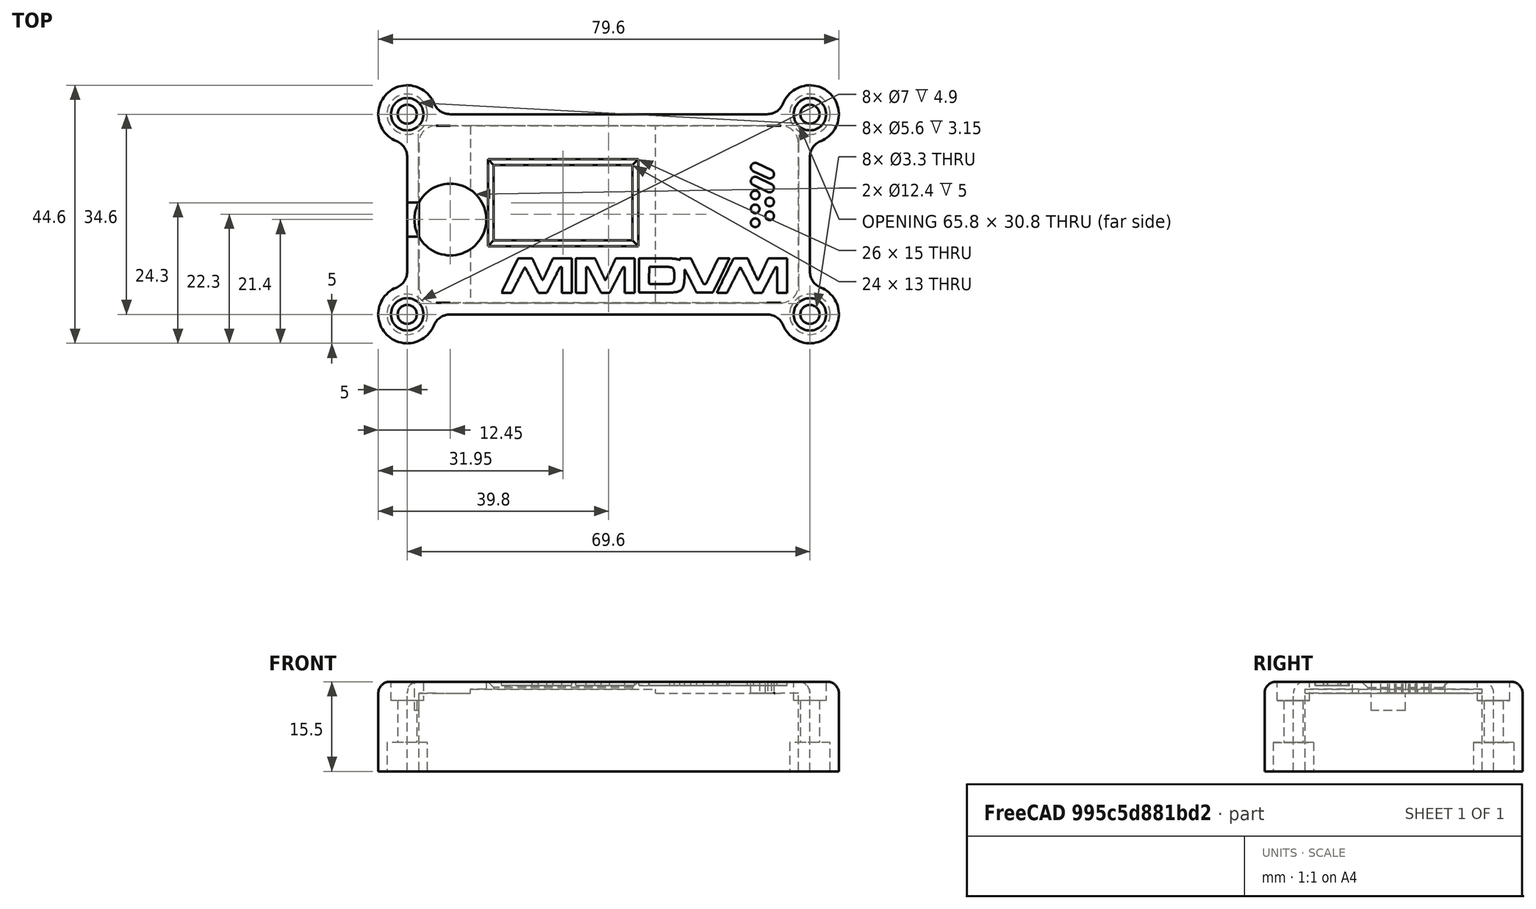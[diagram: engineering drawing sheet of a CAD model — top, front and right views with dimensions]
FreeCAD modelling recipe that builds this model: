
FCSTD DOCUMENT  (FreeCAD 0.18R13830 (Git))
Label: MMDVM_HS_Top-PCB-v1.2-NEW-LEDs
License: CreativeCommons Attribution-NonCommercial-ShareAlike
LicenseURL: http://creativecommons.org/licenses/by-nc-sa/4.0/
objects: Sketcher::SketchObject×11, PartDesign::Pocket×6, Part::Feature×5, PartDesign::Fillet×4, Part::Cut×2, PartDesign::Pad×1, PartDesign::Chamfer×1, PartDesign::Hole×1, Part::MultiFuse×1, Part::FeaturePython×1, Part::Extrusion×1, Mesh::Feature×1, PartDesign::Body×1
note: 43 computed .brp shape members not serialized (recipe doc carries the construction recipe); baked Part::Feature solids carry a one-line shape summary decoded from their .brp

FEATURE [Sketcher::SketchObject] Sketch
  MapMode = 5
  Support = -> [XY_Plane]
  sketch-geometry (24):
    g0: LineSegment [constr] StartX=-32.5 StartY=15 StartZ=0 EndX=32.5 EndY=15 EndZ=0
    g1: LineSegment [constr] StartX=32.5 StartY=15 StartZ=0 EndX=32.5 EndY=-15 EndZ=0
    g2: LineSegment [constr] StartX=32.5 StartY=-15 StartZ=0 EndX=-32.5 EndY=-15 EndZ=0
    g3: LineSegment [constr] StartX=-32.5 StartY=-15 StartZ=0 EndX=-32.5 EndY=15 EndZ=0
    g4: LineSegment [constr] StartX=-29 StartY=11.5 StartZ=0 EndX=29 EndY=11.5 EndZ=0
    g5: LineSegment [constr] StartX=29 StartY=11.5 StartZ=0 EndX=29 EndY=-11.5 EndZ=0
    g6: LineSegment [constr] StartX=29 StartY=-11.5 StartZ=0 EndX=-29 EndY=-11.5 EndZ=0
    g7: LineSegment [constr] StartX=-29 StartY=-11.5 StartZ=0 EndX=-29 EndY=11.5 EndZ=0
    g8: Circle CenterX=-29 CenterY=11.5 CenterZ=0 NormalX=0 NormalY=0 NormalZ=1 AngleXU=0 Radius=1.375
    g9: Circle CenterX=29 CenterY=11.5 CenterZ=0 NormalX=0 NormalY=0 NormalZ=1 AngleXU=0 Radius=1.375
    g10: Circle CenterX=29 CenterY=-11.5 CenterZ=0 NormalX=0 NormalY=0 NormalZ=1 AngleXU=0 Radius=1.375
    g11: Circle CenterX=-29 CenterY=-11.5 CenterZ=0 NormalX=0 NormalY=0 NormalZ=1 AngleXU=0 Radius=1.375
    g12: LineSegment [constr] StartX=-29.5 StartY=12 StartZ=0 EndX=29.5 EndY=12 EndZ=0
    g13: LineSegment [constr] StartX=29.5 StartY=12 StartZ=0 EndX=29.5 EndY=-12 EndZ=0
    g14: LineSegment [constr] StartX=29.5 StartY=-12 StartZ=0 EndX=-29.5 EndY=-12 EndZ=0
    g15: LineSegment [constr] StartX=-29.5 StartY=-12 StartZ=0 EndX=-29.5 EndY=12 EndZ=0
    g16: ArcOfCircle CenterX=-29.5 CenterY=12 CenterZ=0 NormalX=0 NormalY=0 NormalZ=1 AngleXU=0 Radius=3 StartAngle=1.5708 EndAngle=3.1416
    g17: ArcOfCircle CenterX=29.5 CenterY=12 CenterZ=0 NormalX=0 NormalY=0 NormalZ=1 AngleXU=0 Radius=3 StartAngle=1.42077e-07 EndAngle=1.5708
    g18: ArcOfCircle CenterX=29.5 CenterY=-12 CenterZ=0 NormalX=0 NormalY=0 NormalZ=1 AngleXU=0 Radius=3 StartAngle=4.71239 EndAngle=6.28319
    g19: ArcOfCircle CenterX=-29.5 CenterY=-12 CenterZ=0 NormalX=0 NormalY=0 NormalZ=1 AngleXU=0 Radius=3 StartAngle=3.14159 EndAngle=4.71239
    g20: LineSegment StartX=-29.5 StartY=15 StartZ=0 EndX=29.5 EndY=15 EndZ=0
    g21: LineSegment StartX=32.5 StartY=12 StartZ=0 EndX=32.5 EndY=-12 EndZ=0
    g22: LineSegment StartX=29.5 StartY=-15 StartZ=0 EndX=-29.5 EndY=-15 EndZ=0
    g23: LineSegment StartX=-32.5 StartY=-12 StartZ=0 EndX=-32.5 EndY=12 EndZ=0
  constraints (68):
    c: Coincident(g0,g1)
    c: Coincident(g1,g2)
    c: Coincident(g2,g3)
    c: Coincident(g3,g0)
    c: Horizontal(g0)
    c: Horizontal(g2)
    c: Vertical(g1)
    c: Vertical(g3)
    c: DistanceX(g0,g0) = 65
    c: DistanceY(g1,g1) = 30
    c: Symmetric(g0,g0,g-2)
    c: Symmetric(g0,g1,g-1)
    c: Coincident(g4,g5)
    c: Coincident(g5,g6)
    c: Coincident(g6,g7)
    c: Coincident(g7,g4)
    c: Horizontal(g4)
    c: Horizontal(g6)
    c: Vertical(g5)
    c: Vertical(g7)
    c: DistanceX(g4,g4) = 58
    c: DistanceY(g5,g5) = 23
    c: Symmetric(g4,g5,g-1)
    c: Symmetric(g4,g4,g-2)
    c: Coincident(g8,g4)
    c: Coincident(g9,g4)
    c: Coincident(g10,g5)
    c: Coincident(g11,g6)
    c: Radius(g11) = 1.375
    c: Radius(g8) = 1.375
    c: Radius(g9) = 1.375
    c: Radius(g10) = 1.375
    c: Coincident(g12,g13)
    c: Coincident(g13,g14)
    c: Coincident(g14,g15)
    c: Coincident(g15,g12)
    c: Horizontal(g12)
    c: Horizontal(g14)
    c: Vertical(g13)
    c: Vertical(g15)
    c: DistanceX(g4,g12) = 0.5
    c: DistanceY(g4,g12) = 0.5
    c: DistanceY(g13,g5) = 0.5
    c: DistanceX(g14,g6) = 0.5
    c: Coincident(g16,g12)
    c: Radius(g16) = 3
    c: Coincident(g17,g12)
    c: Radius(g17) = 3
    c: Coincident(g18,g13)
    c: Radius(g18) = 3
    c: Coincident(g19,g14)
    c: Radius(g19) = 3
    c: PointOnObject(g16,g0)
    c: PointOnObject(g17,g1)
    c: PointOnObject(g18,g2)
    c: PointOnObject(g19,g3)
    c: Coincident(g20,g16)
    c: Horizontal(g20)
    c: Coincident(g20,g17)
    c: Coincident(g21,g17)
    c: Vertical(g21)
    c: Coincident(g18,g21)
    c: Coincident(g22,g18)
    c: Horizontal(g22)
    c: Coincident(g19,g22)
    c: Coincident(g23,g19)
    c: Vertical(g23)
    c: Coincident(g23,g16)
FEATURE [Sketcher::SketchObject] Sketch001
  MapMode = 5
  Support = -> [XY_Plane]
  expr: Constraints[8] = Sketch.Constraints[8]
  expr: Constraints[41] = Sketch.Constraints[41]
  expr: Constraints[9] = Sketch.Constraints[9]
  expr: Constraints[45] = Sketch.Constraints[45]
  expr: Constraints[43] = Sketch.Constraints[43]
  expr: Constraints[42] = Sketch.Constraints[42]
  expr: Constraints[20] = Sketch.Constraints[20]
  expr: Constraints[21] = Sketch.Constraints[21]
  expr: Constraints[28] = Sketch.Constraints[28]
  expr: Constraints[29] = Sketch.Constraints[29]
  expr: Constraints[30] = Sketch.Constraints[30]
  expr: Constraints[40] = Sketch.Constraints[40]
  expr: Constraints[31] = Sketch.Constraints[31]
  expr: Constraints[47] = Sketch.Constraints[47]
  expr: Constraints[49] = Sketch.Constraints[49]
  expr: Constraints[51] = Sketch.Constraints[51]
  sketch-geometry (64):
    g0: LineSegment [constr] StartX=-32.5 StartY=15 StartZ=0 EndX=32.5 EndY=15 EndZ=0
    g1: LineSegment [constr] StartX=32.5 StartY=15 StartZ=0 EndX=32.5 EndY=-15 EndZ=0
    g2: LineSegment [constr] StartX=32.5 StartY=-15 StartZ=0 EndX=-32.5 EndY=-15 EndZ=0
    g3: LineSegment [constr] StartX=-32.5 StartY=-15 StartZ=0 EndX=-32.5 EndY=15 EndZ=0
    g4: LineSegment [constr] StartX=-29 StartY=11.5 StartZ=0 EndX=29 EndY=11.5 EndZ=0
    g5: LineSegment [constr] StartX=29 StartY=11.5 StartZ=0 EndX=29 EndY=-11.5 EndZ=0
    g6: LineSegment [constr] StartX=29 StartY=-11.5 StartZ=0 EndX=-29 EndY=-11.5 EndZ=0
    g7: LineSegment [constr] StartX=-29 StartY=-11.5 StartZ=0 EndX=-29 EndY=11.5 EndZ=0
    g8: Circle [constr] CenterX=-29 CenterY=11.5 CenterZ=0 NormalX=0 NormalY=0 NormalZ=1 AngleXU=0 Radius=1.375
    g9: Circle [constr] CenterX=29 CenterY=11.5 CenterZ=0 NormalX=0 NormalY=0 NormalZ=1 AngleXU=0 Radius=1.375
    g10: Circle [constr] CenterX=29 CenterY=-11.5 CenterZ=0 NormalX=0 NormalY=0 NormalZ=1 AngleXU=0 Radius=1.375
    g11: Circle [constr] CenterX=-29 CenterY=-11.5 CenterZ=0 NormalX=0 NormalY=0 NormalZ=1 AngleXU=0 Radius=1.375
    g12: LineSegment [constr] StartX=-29.5 StartY=12 StartZ=0 EndX=29.5 EndY=12 EndZ=0
    g13: LineSegment [constr] StartX=29.5 StartY=12 StartZ=0 EndX=29.5 EndY=-12 EndZ=0
    g14: LineSegment [constr] StartX=29.5 StartY=-12 StartZ=0 EndX=-29.5 EndY=-12 EndZ=0
    g15: LineSegment [constr] StartX=-29.5 StartY=-12 StartZ=0 EndX=-29.5 EndY=12 EndZ=0
    g16: ArcOfCircle [constr] CenterX=-29.5 CenterY=12 CenterZ=0 NormalX=0 NormalY=0 NormalZ=1 AngleXU=0 Radius=3 StartAngle=1.5708 EndAngle=3.14159
    g17: ArcOfCircle [constr] CenterX=29.5 CenterY=12 CenterZ=0 NormalX=0 NormalY=0 NormalZ=1 AngleXU=0 Radius=3 StartAngle=2.8425e-08 EndAngle=1.5708
    g18: ArcOfCircle [constr] CenterX=29.5 CenterY=-12 CenterZ=0 NormalX=0 NormalY=0 NormalZ=1 AngleXU=0 Radius=3 StartAngle=4.71239 EndAngle=6.28319
    g19: ArcOfCircle [constr] CenterX=-29.5 CenterY=-12 CenterZ=0 NormalX=0 NormalY=0 NormalZ=1 AngleXU=0 Radius=3 StartAngle=3.14159 EndAngle=4.71239
    g20: LineSegment [constr] StartX=-29.5 StartY=15 StartZ=0 EndX=29.5 EndY=15 EndZ=0
    g21: LineSegment [constr] StartX=32.5 StartY=12 StartZ=0 EndX=32.5 EndY=-12 EndZ=0
    g22: LineSegment [constr] StartX=29.5 StartY=-15 StartZ=0 EndX=-29.5 EndY=-15 EndZ=0
    g23: LineSegment [constr] StartX=-32.5 StartY=-12 StartZ=0 EndX=-32.5 EndY=12 EndZ=0
    g24: ArcOfCircle [constr] CenterX=-29.5 CenterY=12 CenterZ=0 NormalX=0 NormalY=0 NormalZ=1 AngleXU=0 Radius=3.3 StartAngle=1.5708 EndAngle=3.14159
    g25: ArcOfCircle [constr] CenterX=29.5 CenterY=12 CenterZ=0 NormalX=0 NormalY=0 NormalZ=1 AngleXU=0 Radius=3.3 StartAngle=-2.2e-10 EndAngle=1.5708
    g26: ArcOfCircle [constr] CenterX=29.5 CenterY=-12 CenterZ=0 NormalX=0 NormalY=0 NormalZ=1 AngleXU=0 Radius=3.3 StartAngle=4.71239 EndAngle=6.28319
    g27: ArcOfCircle [constr] CenterX=-29.5 CenterY=-12 CenterZ=0 NormalX=0 NormalY=0 NormalZ=1 AngleXU=0 Radius=3.3 StartAngle=3.14159 EndAngle=4.71239
    g28: LineSegment [constr] StartX=-32.8 StartY=12 StartZ=0 EndX=-32.8 EndY=-12 EndZ=0
    g29: LineSegment [constr] StartX=-29.5 StartY=15.3 StartZ=0 EndX=29.5 EndY=15.3 EndZ=0
    g30: LineSegment [constr] StartX=32.8 StartY=12 StartZ=0 EndX=32.8 EndY=-12 EndZ=0
    g31: LineSegment [constr] StartX=29.5 StartY=-15.3 StartZ=0 EndX=-29.5 EndY=-15.3 EndZ=0
    g32: LineSegment [constr] StartX=-34.8 StartY=17.3 StartZ=0 EndX=34.8 EndY=17.3 EndZ=0
    g33: LineSegment [constr] StartX=34.8 StartY=17.3 StartZ=0 EndX=34.8 EndY=-17.3 EndZ=0
    g34: LineSegment [constr] StartX=34.8 StartY=-17.3 StartZ=0 EndX=-34.8 EndY=-17.3 EndZ=0
    g35: LineSegment [constr] StartX=-34.8 StartY=-17.3 StartZ=0 EndX=-34.8 EndY=17.3 EndZ=0
    g36: Circle [constr] CenterX=34.8 CenterY=17.3 CenterZ=0 NormalX=0 NormalY=0 NormalZ=1 AngleXU=0 Radius=5
    g37: Circle [constr] CenterX=34.8 CenterY=-17.3 CenterZ=0 NormalX=0 NormalY=0 NormalZ=1 AngleXU=0 Radius=5
    g38: Circle [constr] CenterX=-34.8 CenterY=-17.3 CenterZ=0 NormalX=0 NormalY=0 NormalZ=1 AngleXU=0 Radius=5
    g39: Circle [constr] CenterX=-34.8 CenterY=17.3 CenterZ=0 NormalX=0 NormalY=0 NormalZ=1 AngleXU=0 Radius=5
    g40: Circle [constr] CenterX=27.3838 CenterY=20.3 CenterZ=0 NormalX=0 NormalY=0 NormalZ=1 AngleXU=0 Radius=3
    g41: Circle [constr] CenterX=-27.3838 CenterY=20.3 CenterZ=0 NormalX=0 NormalY=0 NormalZ=1 AngleXU=0 Radius=3
    g42: Circle [constr] CenterX=-37.8 CenterY=9.8838 CenterZ=0 NormalX=0 NormalY=0 NormalZ=1 AngleXU=0 Radius=3
    g43: Circle [constr] CenterX=-37.8 CenterY=-9.8838 CenterZ=0 NormalX=0 NormalY=0 NormalZ=1 AngleXU=0 Radius=3
    g44: Circle [constr] CenterX=-27.3838 CenterY=-20.3 CenterZ=0 NormalX=0 NormalY=0 NormalZ=1 AngleXU=0 Radius=3
    g45: Circle [constr] CenterX=27.3838 CenterY=-20.3 CenterZ=0 NormalX=0 NormalY=0 NormalZ=1 AngleXU=0 Radius=3
    g46: Circle [constr] CenterX=37.8 CenterY=-9.8838 CenterZ=0 NormalX=0 NormalY=0 NormalZ=1 AngleXU=0 Radius=3
    g47: Circle [constr] CenterX=37.8 CenterY=9.8838 CenterZ=0 NormalX=0 NormalY=0 NormalZ=1 AngleXU=0 Radius=3
    g48: ArcOfCircle CenterX=34.8 CenterY=17.3 CenterZ=0 NormalX=0 NormalY=0 NormalZ=1 AngleXU=0 Radius=5 StartAngle=5.09679 EndAngle=9.04038
    g49: ArcOfCircle CenterX=27.3838 CenterY=20.3 CenterZ=0 NormalX=0 NormalY=0 NormalZ=1 AngleXU=0 Radius=3 StartAngle=4.71239 EndAngle=5.89879
    g50: ArcOfCircle CenterX=37.8 CenterY=9.8838 CenterZ=0 NormalX=0 NormalY=0 NormalZ=1 AngleXU=0 Radius=3 StartAngle=1.95519 EndAngle=3.14159
    g51: ArcOfCircle CenterX=37.8 CenterY=-9.8838 CenterZ=0 NormalX=0 NormalY=0 NormalZ=1 AngleXU=0 Radius=3 StartAngle=3.14159 EndAngle=4.32799
    g52: ArcOfCircle CenterX=34.8 CenterY=-17.3 CenterZ=0 NormalX=0 NormalY=0 NormalZ=1 AngleXU=0 Radius=5 StartAngle=3.52599 EndAngle=7.46958
    g53: ArcOfCircle CenterX=27.3838 CenterY=-20.3 CenterZ=0 NormalX=0 NormalY=0 NormalZ=1 AngleXU=0 Radius=3 StartAngle=0.384397 EndAngle=1.5708
    g54: ArcOfCircle CenterX=-27.3838 CenterY=-20.3 CenterZ=0 NormalX=0 NormalY=0 NormalZ=1 AngleXU=0 Radius=3 StartAngle=1.5708 EndAngle=2.7572
    g55: ArcOfCircle CenterX=-34.8 CenterY=-17.3 CenterZ=0 NormalX=0 NormalY=0 NormalZ=1 AngleXU=0 Radius=5 StartAngle=1.95519 EndAngle=5.89879
    g56: ArcOfCircle CenterX=-37.8 CenterY=-9.8838 CenterZ=0 NormalX=0 NormalY=0 NormalZ=1 AngleXU=0 Radius=3 StartAngle=5.09679 EndAngle=6.28319
    g57: ArcOfCircle CenterX=-37.8 CenterY=9.8838 CenterZ=0 NormalX=0 NormalY=0 NormalZ=1 AngleXU=0 Radius=3 StartAngle=6.28319 EndAngle=7.46958
    g58: ArcOfCircle CenterX=-34.8 CenterY=17.3 CenterZ=0 NormalX=0 NormalY=0 NormalZ=1 AngleXU=0 Radius=5 StartAngle=0.384397 EndAngle=4.32799
    g59: ArcOfCircle CenterX=-27.3838 CenterY=20.3 CenterZ=0 NormalX=0 NormalY=0 NormalZ=1 AngleXU=0 Radius=3 StartAngle=3.52599 EndAngle=4.71239
    g60: LineSegment StartX=-27.3838 StartY=17.3 StartZ=0 EndX=27.3838 EndY=17.3 EndZ=0
    g61: LineSegment StartX=34.8 StartY=9.8838 StartZ=0 EndX=34.8 EndY=-9.8838 EndZ=0
    g62: LineSegment StartX=27.3838 StartY=-17.3 StartZ=0 EndX=-27.3838 EndY=-17.3 EndZ=0
    g63: LineSegment StartX=-34.8 StartY=-9.8838 StartZ=0 EndX=-34.8 EndY=9.8838 EndZ=0
  constraints (184):
    c: Coincident(g0,g1)
    c: Coincident(g1,g2)
    c: Coincident(g2,g3)
    c: Coincident(g3,g0)
    c: Horizontal(g0)
    c: Horizontal(g2)
    c: Vertical(g1)
    c: Vertical(g3)
    c: DistanceX(g0,g0) = 65
    c: DistanceY(g1,g1) = 30
    c: Symmetric(g0,g0,g-2)
    c: Symmetric(g0,g1,g-1)
    c: Coincident(g4,g5)
    c: Coincident(g5,g6)
    c: Coincident(g6,g7)
    c: Coincident(g7,g4)
    c: Horizontal(g4)
    c: Horizontal(g6)
    c: Vertical(g5)
    c: Vertical(g7)
    c: DistanceX(g4,g4) = 58
    c: DistanceY(g5,g5) = 23
    c: Symmetric(g4,g5,g-1)
    c: Symmetric(g4,g4,g-2)
    c: Coincident(g8,g4)
    c: Coincident(g9,g4)
    c: Coincident(g10,g5)
    c: Coincident(g11,g6)
    c: Radius(g11) = 1.375
    c: Radius(g8) = 1.375
    c: Radius(g9) = 1.375
    c: Radius(g10) = 1.375
    c: Coincident(g12,g13)
    c: Coincident(g13,g14)
    c: Coincident(g14,g15)
    c: Coincident(g15,g12)
    c: Horizontal(g12)
    c: Horizontal(g14)
    c: Vertical(g13)
    c: Vertical(g15)
    c: DistanceX(g4,g12) = 0.5
    c: DistanceY(g4,g12) = 0.5
    c: DistanceY(g13,g5) = 0.5
    c: DistanceX(g14,g6) = 0.5
    c: Coincident(g16,g12)
    c: Radius(g16) = 3
    c: Coincident(g17,g12)
    c: Radius(g17) = 3
    c: Coincident(g18,g13)
    c: Radius(g18) = 3
    c: Coincident(g19,g14)
    c: Radius(g19) = 3
    c: PointOnObject(g16,g0)
    c: PointOnObject(g17,g1)
    c: PointOnObject(g18,g2)
    c: PointOnObject(g19,g3)
    c: Coincident(g20,g16)
    c: Horizontal(g20)
    c: Coincident(g20,g17)
    c: Coincident(g21,g17)
    c: Vertical(g21)
    c: Coincident(g18,g21)
    c: Coincident(g22,g18)
    c: Horizontal(g22)
    c: Coincident(g19,g22)
    c: Coincident(g23,g19)
    c: Vertical(g23)
    c: Coincident(g23,g16)
    c: Coincident(g24,g12)
    c: Radius(g24) = 3.3
    c: Coincident(g25,g12)
    c: Radius(g25) = 3.3
    c: Coincident(g26,g13)
    c: Radius(g26) = 3.3
    c: Coincident(g27,g14)
    c: Radius(g27) = 3.3
    c: Vertical(g28)
    c: DistanceX(g28,g2) = 0.3
    c: Coincident(g27,g28)
    c: Coincident(g28,g24)
    c: Horizontal(g29)
    c: DistanceY(g0,g29) = 0.3
    c: Coincident(g24,g29)
    c: Coincident(g25,g29)
    c: Vertical(g30)
    c: DistanceX(g0,g30) = 0.3
    c: Coincident(g25,g30)
    c: Coincident(g30,g26)
    c: Horizontal(g31)
    c: DistanceY(g31,g1) = 0.3
    c: Coincident(g31,g26)
    c: Coincident(g31,g27)
    c: Coincident(g32,g33)
    c: Coincident(g33,g34)
    c: Coincident(g34,g35)
    c: Coincident(g35,g32)
    c: Horizontal(g32)
    c: Horizontal(g34)
    c: Vertical(g33)
    c: Vertical(g35)
    c: DistanceY(g25,g32) = 2
    c: DistanceX(g25,g32) = 2
    c: DistanceY(g33,g26) = 2
    c: DistanceX(g34,g27) = 2
    c: Coincident(g36,g32)
    c: Coincident(g37,g33)
    c: Coincident(g38,g34)
    c: Coincident(g39,g32)
    c: Radius(g39) = 5
    c: Radius(g38) = 5
    c: Radius(g37) = 5
    c: Radius(g36) = 5
    c: Radius(g40) = 3
    c: Tangent(g40,g36)
    c: Tangent(g40,g32)
    c: Tangent(g47,g36)
    c: Radius(g47) = 3
    c: Tangent(g47,g33)
    c: Radius(g46) = 3
    c: Tangent(g46,g37)
    c: Tangent(g46,g33)
    c: Radius(g45) = 3
    c: Tangent(g45,g37)
    c: Tangent(g45,g34)
    c: Radius(g44) = 3
    c: Tangent(g44,g34)
    c: Tangent(g44,g38)
    c: Radius(g43) = 3
    c: Tangent(g43,g38)
    c: Tangent(g43,g35)
    c: Radius(g42) = 3
    c: Tangent(g42,g35)
    c: Tangent(g42,g39)
    c: Radius(g41) = 3
    c: Tangent(g41,g32)
    c: Tangent(g41,g39)
    c: Coincident(g48,g32)
    c: PointOnObject(g48,g36)
    c: Coincident(g49,g40)
    c: PointOnObject(g49,g40)
    c: Coincident(g50,g47)
    c: PointOnObject(g50,g47)
    c: Coincident(g51,g46)
    c: PointOnObject(g51,g46)
    c: Coincident(g52,g33)
    c: PointOnObject(g52,g37)
    c: Coincident(g53,g45)
    c: PointOnObject(g53,g45)
    c: Coincident(g54,g44)
    c: PointOnObject(g54,g44)
    c: Coincident(g55,g34)
    c: PointOnObject(g55,g38)
    c: Coincident(g56,g43)
    c: PointOnObject(g56,g43)
    c: Coincident(g57,g42)
    c: PointOnObject(g57,g42)
    c: Coincident(g58,g32)
    c: PointOnObject(g58,g39)
    c: Coincident(g59,g41)
    c: PointOnObject(g59,g41)
    c: Coincident(g49,g48)
    c: Coincident(g48,g50)
    c: Coincident(g51,g52)
    c: Coincident(g52,g53)
    c: Coincident(g54,g55)
    c: Coincident(g55,g56)
    c: Coincident(g57,g58)
    c: Coincident(g58,g59)
    c: PointOnObject(g60,g32)
    c: Horizontal(g60)
    c: PointOnObject(g61,g33)
    c: Vertical(g61)
    c: PointOnObject(g62,g34)
    c: Horizontal(g62)
    c: PointOnObject(g63,g35)
    c: Vertical(g63)
    c: Coincident(g59,g60)
    c: Coincident(g60,g49)
    c: Coincident(g50,g61)
    c: Coincident(g61,g51)
    c: Coincident(g53,g62)
    c: Coincident(g54,g62)
    c: Coincident(g56,g63)
    c: Coincident(g57,g63)
FEATURE [PartDesign::Pad] Pad
  Length = 15.5
  Length2 = 100
  Profile = -> Sketch001
  Type = 0
FEATURE [Sketcher::SketchObject] Sketch002
  ExternalGeometry = -> [Pad]
  MapMode = 5
  Placement = pos=(0,0,0) rot=(1,0,0;3.14159rad)
  Support = -> [Pad]
  sketch-geometry (4):
    g0: Circle CenterX=34.8 CenterY=17.3 CenterZ=0 NormalX=0 NormalY=0 NormalZ=1 AngleXU=0 Radius=3.5
    g1: Circle CenterX=34.8 CenterY=-17.3 CenterZ=0 NormalX=0 NormalY=0 NormalZ=1 AngleXU=0 Radius=3.5
    g2: Circle CenterX=-34.8 CenterY=-17.3 CenterZ=0 NormalX=0 NormalY=0 NormalZ=1 AngleXU=0 Radius=3.5
    g3: Circle CenterX=-34.8 CenterY=17.3 CenterZ=0 NormalX=0 NormalY=0 NormalZ=1 AngleXU=0 Radius=3.5
  constraints (8):
    c: Coincident(g0,g-3)
    c: Radius(g0) = 3.5
    c: Coincident(g1,g-6)
    c: Radius(g1) = 3.5
    c: Coincident(g2,g-5)
    c: Radius(g2) = 3.5
    c: Coincident(g3,g-4)
    c: Radius(g3) = 3.5
FEATURE [PartDesign::Pocket] Pocket
  BaseFeature = -> Pad
  Length = 5
  Length2 = 100
  Profile = -> Sketch002
  Type = 0
FEATURE [Sketcher::SketchObject] Sketch003
  MapMode = 5
  Placement = pos=(0,0,0) rot=(1,0,0;3.14159rad)
  Support = -> [Pocket]
  expr: Constraints[8] = Sketch.Constraints[8]
  expr: Constraints[39] = Sketch.Constraints[40]
  expr: Constraints[30] = Sketch.Constraints[31]
  expr: Constraints[27] = Sketch.Constraints[28]
  expr: Constraints[29] = Sketch.Constraints[30]
  expr: Constraints[28] = Sketch.Constraints[29]
  expr: Constraints[20] = -Sketch.Constraints[21]
  expr: Constraints[19] = Sketch.Constraints[20]
  expr: Constraints[42] = Sketch.Constraints[43]
  expr: Constraints[41] = -Sketch.Constraints[42]
  expr: Constraints[9] = -Sketch.Constraints[9]
  expr: Constraints[40] = -Sketch.Constraints[41]
  sketch-geometry (32):
    g0: LineSegment [constr] StartX=-32.5 StartY=-15 StartZ=0 EndX=32.5 EndY=-15 EndZ=0
    g1: LineSegment [constr] StartX=32.5 StartY=-15 StartZ=0 EndX=32.5 EndY=15 EndZ=0
    g2: LineSegment [constr] StartX=32.5 StartY=15 StartZ=0 EndX=-32.5 EndY=15 EndZ=0
    g3: LineSegment [constr] StartX=-32.5 StartY=15 StartZ=0 EndX=-32.5 EndY=-15 EndZ=0
    g4: LineSegment [constr] StartX=-29 StartY=-11.5 StartZ=0 EndX=29 EndY=-11.5 EndZ=0
    g5: LineSegment [constr] StartX=29 StartY=-11.5 StartZ=0 EndX=29 EndY=11.5 EndZ=0
    g6: LineSegment [constr] StartX=29 StartY=11.5 StartZ=0 EndX=-29 EndY=11.5 EndZ=0
    g7: LineSegment [constr] StartX=-29 StartY=11.5 StartZ=0 EndX=-29 EndY=-11.5 EndZ=0
    g8: Circle [constr] CenterX=-29 CenterY=-11.5 CenterZ=0 NormalX=0 NormalY=0 NormalZ=1 AngleXU=0 Radius=1.375
    g9: Circle [constr] CenterX=29 CenterY=-11.5 CenterZ=0 NormalX=0 NormalY=0 NormalZ=1 AngleXU=0 Radius=1.375
    g10: Circle [constr] CenterX=29 CenterY=11.5 CenterZ=0 NormalX=0 NormalY=0 NormalZ=1 AngleXU=0 Radius=1.375
    g11: Circle [constr] CenterX=-29 CenterY=11.5 CenterZ=0 NormalX=0 NormalY=0 NormalZ=1 AngleXU=0 Radius=1.375
    g12: LineSegment [constr] StartX=-29.5 StartY=-12 StartZ=0 EndX=29.5 EndY=-12 EndZ=0
    g13: LineSegment [constr] StartX=29.5 StartY=-12 StartZ=0 EndX=29.5 EndY=12 EndZ=0
    g14: LineSegment [constr] StartX=29.5 StartY=12 StartZ=0 EndX=-29.5 EndY=12 EndZ=0
    g15: LineSegment [constr] StartX=-29.5 StartY=12 StartZ=0 EndX=-29.5 EndY=-12 EndZ=0
    g16: LineSegment [constr] StartX=-29.5121 StartY=-15 StartZ=0 EndX=29.5 EndY=-15 EndZ=0
    g17: LineSegment [constr] StartX=32.5 StartY=-12 StartZ=0 EndX=32.5 EndY=12 EndZ=0
    g18: LineSegment [constr] StartX=29.5 StartY=15 StartZ=0 EndX=-29.5121 EndY=15 EndZ=0
    g19: LineSegment [constr] StartX=-32.5 StartY=12 StartZ=0 EndX=-32.5 EndY=-12 EndZ=0
    g20: ArcOfCircle [constr] CenterX=-29.5 CenterY=12 CenterZ=0 NormalX=0 NormalY=0 NormalZ=1 AngleXU=0 Radius=3.00002 StartAngle=1.57483 EndAngle=3.1416
    g21: ArcOfCircle [constr] CenterX=29.5 CenterY=12 CenterZ=0 NormalX=0 NormalY=0 NormalZ=1 AngleXU=0 Radius=3 StartAngle=6.28318 EndAngle=7.85399
    g22: ArcOfCircle [constr] CenterX=29.5 CenterY=-12 CenterZ=0 NormalX=0 NormalY=0 NormalZ=1 AngleXU=0 Radius=3 StartAngle=4.71238 EndAngle=6.28319
    g23: ArcOfCircle [constr] CenterX=-29.5 CenterY=-12 CenterZ=0 NormalX=0 NormalY=0 NormalZ=1 AngleXU=0 Radius=3.00002 StartAngle=3.14159 EndAngle=4.70836
    g24: LineSegment StartX=-29.8 StartY=15.3 StartZ=0 EndX=29.8 EndY=15.3 EndZ=0
    g25: LineSegment StartX=32.8 StartY=12.3 StartZ=0 EndX=32.8 EndY=-12.3 EndZ=0
    g26: LineSegment StartX=29.8 StartY=-15.3 StartZ=0 EndX=-29.8 EndY=-15.3 EndZ=0
    g27: LineSegment StartX=-32.8 StartY=-12.3 StartZ=0 EndX=-32.8 EndY=12.3 EndZ=0
    g28: ArcOfCircle CenterX=29.8 CenterY=12.3 CenterZ=0 NormalX=0 NormalY=0 NormalZ=1 AngleXU=0 Radius=3 StartAngle=0 EndAngle=1.5708
    g29: ArcOfCircle CenterX=29.8 CenterY=-12.3 CenterZ=0 NormalX=0 NormalY=0 NormalZ=1 AngleXU=0 Radius=3 StartAngle=4.71239 EndAngle=6.28319
    g30: ArcOfCircle CenterX=-29.8 CenterY=-12.3 CenterZ=0 NormalX=0 NormalY=0 NormalZ=1 AngleXU=0 Radius=3 StartAngle=3.14159 EndAngle=4.71239
    g31: ArcOfCircle CenterX=-29.8 CenterY=12.3 CenterZ=0 NormalX=0 NormalY=0 NormalZ=1 AngleXU=0 Radius=3 StartAngle=1.5708 EndAngle=3.14159
  constraints (83):
    c: Coincident(g0,g1)
    c: Coincident(g1,g2)
    c: Coincident(g2,g3)
    c: Coincident(g3,g0)
    c: Horizontal(g0)
    c: Horizontal(g2)
    c: Vertical(g1)
    c: Vertical(g3)
    c: DistanceX(g0,g0) = 65
    c: DistanceY(g1,g1) = -30
    c: Symmetric(g0,g0,g-2)
    c: Symmetric(g0,g1,g-1)
    c: Coincident(g4,g5)
    c: Coincident(g5,g6)
    c: Coincident(g6,g7)
    c: Horizontal(g4)
    c: Horizontal(g6)
    c: Vertical(g5)
    c: Vertical(g7)
    c: DistanceX(g4,g4) = 58
    c: DistanceY(g5,g5) = -23
    c: Symmetric(g4,g5,g-1)
    c: Symmetric(g4,g4,g-2)
    c: Coincident(g8,g4)
    c: Coincident(g9,g4)
    c: Coincident(g10,g5)
    c: Coincident(g11,g6)
    c: Radius(g11) = 1.375
    c: Radius(g8) = 1.375
    c: Radius(g9) = 1.375
    c: Radius(g10) = 1.375
    c: Coincident(g12,g13)
    c: Coincident(g13,g14)
    c: Coincident(g14,g15)
    c: Coincident(g15,g12)
    c: Horizontal(g12)
    c: Horizontal(g14)
    c: Vertical(g13)
    c: Vertical(g15)
    c: DistanceX(g4,g12) = 0.5
    c: DistanceY(g4,g12) = -0.5
    c: DistanceY(g13,g5) = -0.5
    c: DistanceX(g14,g6) = 0.5
    c: PointOnObject(g16,g0)
    c: PointOnObject(g17,g1)
    c: PointOnObject(g18,g2)
    c: PointOnObject(g19,g3)
    c: Horizontal(g16)
    c: Vertical(g17)
    c: Horizontal(g18)
    c: Vertical(g19)
    c: Coincident(g20,g14)
    c: Coincident(g20,g18)
    c: Coincident(g20,g19)
    c: Coincident(g21,g13)
    c: Coincident(g21,g17)
    c: Coincident(g21,g18)
    c: Coincident(g22,g12)
    c: Coincident(g22,g16)
    c: Coincident(g22,g17)
    c: Coincident(g23,g12)
    c: Coincident(g23,g19)
    c: Coincident(g23,g16)
    c: Horizontal(g24)
    c: Horizontal(g26)
    c: Vertical(g25)
    c: Vertical(g27)
    c: Tangent(g24,g28) = 1.5708
    c: Tangent(g25,g28) = 1.5708
    c: Tangent(g25,g29) = 1.5708
    c: Tangent(g26,g29) = 1.5708
    c: Tangent(g26,g30) = 1.5708
    c: Tangent(g27,g30) = 1.5708
    c: Tangent(g27,g31) = 1.5708
    c: Tangent(g24,g31) = 1.5708
    c: Radius(g31) = 3
    c: Radius(g28) = 3
    c: Radius(g29) = 3
    c: Radius(g30) = 3
    c: DistanceY(g1,g24) = 0.3
    c: DistanceX(g17,g25) = 0.3
    c: DistanceY(g26,g16) = 0.3
    c: DistanceX(g27,g19) = 0.3
FEATURE [PartDesign::Pocket] Pocket001
  BaseFeature = -> Pocket
  Length = 13.5
  Length2 = 100
  Profile = -> Sketch003
  Type = 0
FEATURE [Sketcher::SketchObject] Sketch004
  ExternalGeometry = -> [Pocket001]
  MapMode = 5
  Placement = pos=(0,0,15.5) rot=(0,0,1;0rad)
  Support = -> [Pocket001]
  sketch-geometry (32):
    g0: LineSegment StartX=-27.3838 StartY=17.3 StartZ=0 EndX=-31.8 EndY=17.3 EndZ=0
    g1: LineSegment StartX=-34.8 StartY=9.8838 StartZ=0 EndX=-34.8 EndY=14.3 EndZ=0
    g2: Circle [constr] CenterX=-31.8 CenterY=14.3 CenterZ=0 NormalX=0 NormalY=0 NormalZ=1 AngleXU=0 Radius=3
    g3: ArcOfCircle CenterX=-31.8 CenterY=14.3 CenterZ=0 NormalX=0 NormalY=0 NormalZ=1 AngleXU=0 Radius=3 StartAngle=1.5708 EndAngle=3.14159
    g4: LineSegment StartX=-41.7809 StartY=24.2149 StartZ=0 EndX=-27.3838 EndY=24.2149 EndZ=0
    g5: LineSegment StartX=-41.7809 StartY=9.8838 StartZ=0 EndX=-41.7809 EndY=24.2149 EndZ=0
    g6: LineSegment StartX=-27.3838 StartY=24.2149 StartZ=0 EndX=-27.3838 EndY=17.3 EndZ=0
    g7: LineSegment StartX=-41.7809 StartY=9.8838 StartZ=0 EndX=-34.8 EndY=9.8838 EndZ=0
    g8: LineSegment StartX=27.3838 StartY=17.3 StartZ=0 EndX=31.8 EndY=17.3 EndZ=0
    g9: LineSegment StartX=34.8 StartY=9.8838 StartZ=0 EndX=34.8 EndY=14.3 EndZ=0
    g10: Circle [constr] CenterX=31.8 CenterY=14.3 CenterZ=0 NormalX=0 NormalY=0 NormalZ=1 AngleXU=0 Radius=3
    g11: ArcOfCircle CenterX=31.8 CenterY=14.3 CenterZ=0 NormalX=0 NormalY=0 NormalZ=1 AngleXU=0 Radius=3 StartAngle=4.4834e-08 EndAngle=1.5708
    g12: LineSegment StartX=41.7622 StartY=24.6512 StartZ=0 EndX=27.3838 EndY=24.6512 EndZ=0
    g13: LineSegment StartX=41.7622 StartY=9.8838 StartZ=0 EndX=41.7622 EndY=24.6512 EndZ=0
    g14: LineSegment StartX=27.3838 StartY=24.6512 StartZ=0 EndX=27.3838 EndY=17.3 EndZ=0
    g15: LineSegment StartX=41.7622 StartY=9.8838 StartZ=0 EndX=34.8 EndY=9.8838 EndZ=0
    g16: LineSegment StartX=-34.8 StartY=-9.8838 StartZ=0 EndX=-34.8 EndY=-14.3 EndZ=0
    g17: LineSegment StartX=-27.3838 StartY=-17.3 StartZ=0 EndX=-31.8 EndY=-17.3 EndZ=0
    g18: Circle [constr] CenterX=-31.8 CenterY=-14.3 CenterZ=0 NormalX=0 NormalY=0 NormalZ=1 AngleXU=0 Radius=3
    g19: ArcOfCircle CenterX=-31.8 CenterY=-14.3 CenterZ=0 NormalX=0 NormalY=0 NormalZ=1 AngleXU=0 Radius=3 StartAngle=3.14159 EndAngle=4.71239
    g20: LineSegment StartX=-27.3838 StartY=-24.2044 StartZ=0 EndX=-41.4724 EndY=-24.2044 EndZ=0
    g21: LineSegment StartX=-41.4724 StartY=-24.2044 StartZ=0 EndX=-41.4724 EndY=-9.8838 EndZ=0
    g22: LineSegment StartX=-41.4724 StartY=-9.8838 StartZ=0 EndX=-34.8 EndY=-9.8838 EndZ=0
    g23: LineSegment StartX=-27.3838 StartY=-24.2044 StartZ=0 EndX=-27.3838 EndY=-17.3 EndZ=0
    g24: LineSegment StartX=34.8 StartY=-9.8838 StartZ=0 EndX=34.8 EndY=-14.3 EndZ=0
    g25: LineSegment StartX=27.3838 StartY=-17.3 StartZ=0 EndX=31.8 EndY=-17.3 EndZ=0
    g26: Circle [constr] CenterX=31.8 CenterY=-14.3 CenterZ=0 NormalX=0 NormalY=0 NormalZ=1 AngleXU=0 Radius=3
    g27: ArcOfCircle CenterX=31.8 CenterY=-14.3 CenterZ=0 NormalX=0 NormalY=0 NormalZ=1 AngleXU=0 Radius=3 StartAngle=4.71239 EndAngle=6.28319
    g28: LineSegment StartX=41.5436 StartY=-23.6904 StartZ=0 EndX=27.3838 EndY=-23.6904 EndZ=0
    g29: LineSegment StartX=41.5436 StartY=-9.8838 StartZ=0 EndX=41.5436 EndY=-23.6904 EndZ=0
    g30: LineSegment StartX=41.5436 StartY=-9.8838 StartZ=0 EndX=34.8 EndY=-9.8838 EndZ=0
    g31: LineSegment StartX=27.3838 StartY=-23.6904 StartZ=0 EndX=27.3838 EndY=-17.3 EndZ=0
  constraints (88):
    c: PointOnObject(g0,g-3)
    c: Horizontal(g0)
    c: PointOnObject(g1,g-6)
    c: Vertical(g1)
    c: Radius(g2) = 3
    c: Tangent(g2,g0)
    c: Tangent(g2,g1)
    c: Coincident(g3,g2)
    c: PointOnObject(g3,g2)
    c: Coincident(g3,g1)
    c: Coincident(g3,g0)
    c: Coincident(g5,g4)
    c: Horizontal(g4)
    c: Vertical(g5)
    c: Coincident(g6,g4)
    c: Vertical(g6)
    c: Coincident(g7,g5)
    c: Horizontal(g7)
    c: Coincident(g7,g1)
    c: Coincident(g6,g0)
    c: PointOnObject(g8,g-3)
    c: Horizontal(g8)
    c: PointOnObject(g9,g-4)
    c: Vertical(g9)
    c: Radius(g10) = 3
    c: Tangent(g10,g8)
    c: Tangent(g10,g9)
    c: Coincident(g11,g10)
    c: PointOnObject(g11,g10)
    c: Coincident(g11,g8)
    c: Coincident(g11,g9)
    c: Coincident(g13,g12)
    c: Horizontal(g12)
    c: Vertical(g13)
    c: Coincident(g14,g12)
    c: Vertical(g14)
    c: Coincident(g15,g13)
    c: Horizontal(g15)
    c: Coincident(g15,g9)
    c: Coincident(g14,g8)
    c: PointOnObject(g16,g-6)
    c: Vertical(g16)
    c: PointOnObject(g17,g-5)
    c: Horizontal(g17)
    c: Radius(g18) = 3
    c: Tangent(g18,g16)
    c: Tangent(g18,g17)
    c: Coincident(g19,g18)
    c: PointOnObject(g19,g18)
    c: Coincident(g19,g17)
    c: Coincident(g19,g16)
    c: Coincident(g20,g21)
    c: Horizontal(g20)
    c: Vertical(g21)
    c: Coincident(g22,g21)
    c: Horizontal(g22)
    c: Coincident(g23,g20)
    c: Vertical(g23)
    c: Coincident(g23,g17)
    c: Coincident(g22,g16)
    c: PointOnObject(g24,g-4)
    c: Vertical(g24)
    c: PointOnObject(g25,g-5)
    c: Horizontal(g25)
    c: Radius(g26) = 3
    c: Tangent(g26,g24)
    c: Tangent(g26,g25)
    c: Coincident(g27,g26)
    c: PointOnObject(g27,g26)
    c: Coincident(g27,g24)
    c: Coincident(g27,g25)
    c: Coincident(g29,g28)
    c: Horizontal(g28)
    c: Vertical(g29)
    c: Coincident(g30,g29)
    c: Horizontal(g30)
    c: Coincident(g31,g28)
    c: Vertical(g31)
    c: Coincident(g31,g25)
    c: Coincident(g30,g24)
    c: Coincident(g0,g-3)
    c: Coincident(g1,g-6)
    c: Coincident(g-6,g16)
    c: Coincident(g17,g-5)
    c: Coincident(g-5,g25)
    c: Coincident(g-4,g24)
    c: Coincident(g9,g-4)
    c: Coincident(g8,g-3)
FEATURE [Sketcher::SketchObject] Sketch005
  ExternalGeometry = -> [Pocket001,Sketch]
  MapMode = 5
  Placement = pos=(0,0,15.5) rot=(0,0,1;0rad)
  Support = -> [Pocket001]
  sketch-geometry (10):
    g0: LineSegment [constr] StartX=-27.35 StartY=31.2328 StartZ=0 EndX=-27.35 EndY=-27.0552 EndZ=0
    g1: LineSegment [constr] StartX=-45.4064 StartY=-0.9 StartZ=0 EndX=40.4454 EndY=-0.9 EndZ=0
    g2: Circle [constr] CenterX=-27.35 CenterY=-0.9 CenterZ=0 NormalX=0 NormalY=0 NormalZ=1 AngleXU=0 Radius=6.2
    g3: LineSegment StartX=-19.85 StartY=8.5 StartZ=0 EndX=4.15 EndY=8.5 EndZ=0
    g4: LineSegment StartX=4.15 StartY=8.5 StartZ=0 EndX=4.15 EndY=-4.5 EndZ=0
    g5: LineSegment StartX=4.15 StartY=-4.5 StartZ=0 EndX=-19.85 EndY=-4.5 EndZ=0
    g6: LineSegment StartX=-19.85 StartY=-4.5 StartZ=0 EndX=-19.85 EndY=8.5 EndZ=0
    g7: LineSegment [constr] StartX=-29 StartY=24.9491 StartZ=0 EndX=-29 EndY=-20.674 EndZ=0
    g8: LineSegment [constr] StartX=-44.8443 StartY=11.5 StartZ=0 EndX=14.9752 EndY=11.5 EndZ=0
    g9: Circle CenterX=-27.35 CenterY=-0.9 CenterZ=0 NormalX=0 NormalY=0 NormalZ=1 AngleXU=0 Radius=6.2
  constraints (21):
    c: Coincident(g5,g6)
    c: Coincident(g3,g6)
    c: Coincident(g4,g5)
    c: Coincident(g3,g4)
    c: DistanceX(g3,g3) = 24
    c: DistanceY(g4,g4) = 13
    c: Vertical(g7)
    c: Horizontal(g8)
    c: PointOnObject(g-4,g8)
    c: PointOnObject(g-4,g7)
    c: PointOnObject(g2,g0)
    c: PointOnObject(g2,g1)
    c: DistanceX(g7,g0) = 1.65
    c: DistanceX(g7,g3) = 9.15
    c: DistanceY(g3,g-4) = 3
    c: DistanceY(g1,g8) = 12.4
    c: Vertical(g0)
    c: Horizontal(g1)
    c: Radius(g2) = 6.2
    c: Coincident(g9,g2)
    c: Radius(g9) = 6.2
FEATURE [PartDesign::Pocket] Pocket002
  BaseFeature = -> Pocket001
  Length = 5
  Length2 = 100
  Profile = -> Sketch005
  Type = 0
FEATURE [Sketcher::SketchObject] Sketch006
  ExternalGeometry = -> [Pocket002]
  MapMode = 5
  Placement = pos=(0,0,13.5) rot=(1,0,0;3.14159rad)
  Support = -> [Pocket002]
  sketch-geometry (4):
    g0: LineSegment StartX=-23.85 StartY=15.3 StartZ=0 EndX=8.15 EndY=15.3 EndZ=0
    g1: LineSegment StartX=8.15 StartY=15.3 StartZ=0 EndX=8.15 EndY=-15.3 EndZ=0
    g2: LineSegment StartX=8.15 StartY=-15.3 StartZ=0 EndX=-23.85 EndY=-15.3 EndZ=0
    g3: LineSegment StartX=-23.85 StartY=-15.3 StartZ=0 EndX=-23.85 EndY=15.3 EndZ=0
FEATURE [PartDesign::Pocket] Pocket003
  BaseFeature = -> Pocket002
  Length = 0.7
  Length2 = 100
  Profile = -> Sketch006
  Type = 0
FEATURE [PartDesign::Fillet] Fillet
  Base = -> Pocket003 [Edge38]
  BaseFeature = -> Pocket003
  Radius = 2
FEATURE [PartDesign::Chamfer] Chamfer
  Base = -> Fillet [Edge60,Edge61,Edge62,Edge63]
  BaseFeature = -> Fillet
  Size = 1
FEATURE [Sketcher::SketchObject] Sketch007
  MapMode = 5
  Placement = pos=(0,0,15.5) rot=(0,0,1;0rad)
  sketch-geometry (4):
    g0: Circle CenterX=34.8 CenterY=17.3 CenterZ=0 NormalX=0 NormalY=0 NormalZ=1 AngleXU=0 Radius=2.63102
    g1: Circle CenterX=-34.8 CenterY=17.3 CenterZ=0 NormalX=0 NormalY=0 NormalZ=1 AngleXU=0 Radius=2.66333
    g2: Circle CenterX=-34.8 CenterY=-17.3 CenterZ=0 NormalX=0 NormalY=0 NormalZ=1 AngleXU=0 Radius=2.82775
    g3: Circle CenterX=34.8 CenterY=-17.3 CenterZ=0 NormalX=0 NormalY=0 NormalZ=1 AngleXU=0 Radius=2.89107
FEATURE [PartDesign::Hole] Hole
  BaseFeature = -> Chamfer
  Depth = 20
  DepthType = 1
  Diameter = 3.3
  DrillPoint = 1
  DrillPointAngle = 118
  HoleCutCountersinkAngle = 90
  HoleCutDepth = 0
  HoleCutDiameter = 3
  HoleCutType = 0
  ModelActualThread = false
  Profile = -> Sketch007
  Tapered = false
  TaperedAngle = 90
  ThreadAngle = 60
  ThreadClass = 0
  ThreadCutOffInner = 0.0433013
  ThreadCutOffOuter = 0.0866025
  ThreadDirection = 0
  ThreadFit = 0
  ThreadPitch = 0.4
  ThreadSize = 3
  ThreadType = 1
  Threaded = false
FEATURE [Sketcher::SketchObject] Sketch008
  ExternalGeometry = -> [Hole]
  MapMode = 5
  Placement = pos=(0,0,15.5) rot=(0,0,1;0rad)
  Support = -> [Hole]
  sketch-geometry (4):
    g0: Circle CenterX=34.8 CenterY=17.3 CenterZ=0 NormalX=0 NormalY=0 NormalZ=1 AngleXU=0 Radius=2.8
    g1: Circle CenterX=34.8 CenterY=-17.3 CenterZ=0 NormalX=0 NormalY=0 NormalZ=1 AngleXU=0 Radius=2.8
    g2: Circle CenterX=-34.8 CenterY=-17.3 CenterZ=0 NormalX=0 NormalY=0 NormalZ=1 AngleXU=0 Radius=2.8
    g3: Circle CenterX=-34.8 CenterY=17.3 CenterZ=0 NormalX=0 NormalY=0 NormalZ=1 AngleXU=0 Radius=2.8
  constraints (7):
    c: Coincident(g0,g-5)
    c: Coincident(g1,g-8)
    c: Coincident(g3,g-6)
    c: Radius(g3) = 2.8
    c: Radius(g0) = 2.8
    c: Radius(g2) = 2.8
    c: Radius(g1) = 2.8
FEATURE [PartDesign::Pocket] Pocket004
  BaseFeature = -> Hole
  Length = 3.3
  Length2 = 100
  Profile = -> Sketch008
  Type = 0
FEATURE [PartDesign::Fillet] Fillet002
  Base = -> Pocket004 [Edge23,Edge22,Edge20,Edge21]
  BaseFeature = -> Pocket004
  Radius = 0.15
FEATURE [Sketcher::SketchObject] Sketch009
  MapMode = 5
  Placement = pos=(0,0,15.5) rot=(0,0,1;0rad)
  Support = -> [Fillet002]
  expr: Constraints[7] = Sketch.Constraints[9]
  expr: Constraints[40] = Sketch.Constraints[42]
  expr: Constraints[18] = Sketch.Constraints[20]
  expr: Constraints[19] = Sketch.Constraints[21]
  expr: Constraints[29] = Sketch.Constraints[31]
  expr: Constraints[27] = Sketch.Constraints[29]
  expr: Constraints[28] = Sketch.Constraints[30]
  expr: Constraints[26] = Sketch.Constraints[28]
  expr: Constraints[6] = Sketch.Constraints[8]
  expr: Constraints[38] = Sketch.Constraints[40]
  expr: Constraints[47] = Sketch.Constraints[49]
  expr: Constraints[39] = Sketch.Constraints[41]
  expr: Constraints[49] = Sketch.Constraints[51]
  expr: Constraints[45] = Sketch.Constraints[47]
  expr: Constraints[43] = Sketch.Constraints[45]
  expr: Constraints[41] = Sketch.Constraints[43]
  sketch-geometry (34):
    g0: LineSegment [constr] StartX=-32.5 StartY=15 StartZ=0 EndX=32.5 EndY=15 EndZ=0
    g1: LineSegment [constr] StartX=32.5 StartY=15 StartZ=0 EndX=32.5 EndY=-15 EndZ=0
    g2: LineSegment [constr] StartX=32.5 StartY=-15 StartZ=0 EndX=-32.5 EndY=-15 EndZ=0
    g3: LineSegment [constr] StartX=-32.5 StartY=-15 StartZ=0 EndX=-32.5 EndY=15 EndZ=0
    g4: LineSegment [constr] StartX=-29 StartY=11.5 StartZ=0 EndX=29 EndY=11.5 EndZ=0
    g5: LineSegment [constr] StartX=29 StartY=11.5 StartZ=0 EndX=29 EndY=-11.5 EndZ=0
    g6: LineSegment [constr] StartX=29 StartY=-11.5 StartZ=0 EndX=-29 EndY=-11.5 EndZ=0
    g7: LineSegment [constr] StartX=-29 StartY=-11.5 StartZ=0 EndX=-29 EndY=11.5 EndZ=0
    g8: Circle [constr] CenterX=-29 CenterY=11.5 CenterZ=0 NormalX=0 NormalY=0 NormalZ=1 AngleXU=0 Radius=1.375
    g9: Circle [constr] CenterX=29 CenterY=11.5 CenterZ=0 NormalX=0 NormalY=0 NormalZ=1 AngleXU=0 Radius=1.375
    g10: Circle [constr] CenterX=29 CenterY=-11.5 CenterZ=0 NormalX=0 NormalY=0 NormalZ=1 AngleXU=0 Radius=1.375
    g11: Circle [constr] CenterX=-29 CenterY=-11.5 CenterZ=0 NormalX=0 NormalY=0 NormalZ=1 AngleXU=0 Radius=1.375
    g12: LineSegment [constr] StartX=-29.5 StartY=12 StartZ=0 EndX=29.5 EndY=12 EndZ=0
    g13: LineSegment [constr] StartX=29.5 StartY=12 StartZ=0 EndX=29.5 EndY=-12 EndZ=0
    g14: LineSegment [constr] StartX=29.5 StartY=-12 StartZ=0 EndX=-29.5 EndY=-12 EndZ=0
    g15: LineSegment [constr] StartX=-29.5 StartY=-12 StartZ=0 EndX=-29.5 EndY=12 EndZ=0
    g16: ArcOfCircle [constr] CenterX=-29.5 CenterY=12 CenterZ=0 NormalX=0 NormalY=0 NormalZ=1 AngleXU=0 Radius=3 StartAngle=1.5708 EndAngle=3.14159
    g17: ArcOfCircle [constr] CenterX=29.5 CenterY=12 CenterZ=0 NormalX=0 NormalY=0 NormalZ=1 AngleXU=0 Radius=3 StartAngle=3.9602e-08 EndAngle=1.5708
    g18: ArcOfCircle [constr] CenterX=29.5 CenterY=-12 CenterZ=0 NormalX=0 NormalY=0 NormalZ=1 AngleXU=0 Radius=3 StartAngle=4.71239 EndAngle=6.28319
    g19: ArcOfCircle [constr] CenterX=-29.5 CenterY=-12 CenterZ=0 NormalX=0 NormalY=0 NormalZ=1 AngleXU=0 Radius=3 StartAngle=3.14159 EndAngle=4.71239
    g20: LineSegment [constr] StartX=-29.5 StartY=15 StartZ=0 EndX=29.5 EndY=15 EndZ=0
    g21: LineSegment [constr] StartX=32.5 StartY=12 StartZ=0 EndX=32.5 EndY=-12 EndZ=0
    g22: LineSegment [constr] StartX=29.5 StartY=-15 StartZ=0 EndX=-29.5 EndY=-15 EndZ=0
    g23: LineSegment [constr] StartX=-32.5 StartY=-12 StartZ=0 EndX=-32.5 EndY=12 EndZ=0
    g24: LineSegment [constr] StartX=26.4 StartY=27.403 StartZ=0 EndX=26.4 EndY=-26.3119 EndZ=0
    g25: ArcOfCircle CenterX=26.4 CenterY=8.09 CenterZ=0 NormalX=0 NormalY=0 NormalZ=1 AngleXU=0 Radius=0.75 StartAngle=0 EndAngle=3.14159
    g26: ArcOfCircle CenterX=26.4 CenterY=-1.41 CenterZ=0 NormalX=0 NormalY=0 NormalZ=1 AngleXU=0 Radius=0.75 StartAngle=3.14159 EndAngle=6.28319
    g27: LineSegment StartX=25.65 StartY=8.09 StartZ=0 EndX=25.65 EndY=-1.41 EndZ=0
    g28: LineSegment StartX=27.15 StartY=8.09 StartZ=0 EndX=27.15 EndY=-1.41 EndZ=0
    g29: LineSegment [constr] StartX=36.6897 StartY=3.34 StartZ=0 EndX=15.0074 EndY=3.34 EndZ=0
    g30: LineSegment [constr] StartX=25.4202 StartY=8.84 StartZ=0 EndX=27.4202 EndY=8.84 EndZ=0
    g31: LineSegment [constr] StartX=27.4202 StartY=8.84 StartZ=0 EndX=27.4202 EndY=-2.16 EndZ=0
    g32: LineSegment [constr] StartX=27.4202 StartY=-2.16 StartZ=0 EndX=25.4202 EndY=-2.16 EndZ=0
    g33: LineSegment [constr] StartX=25.4202 StartY=-2.16 StartZ=0 EndX=25.4202 EndY=8.84 EndZ=0
  constraints (91):
    c: Coincident(g0,g1)
    c: Coincident(g1,g2)
    c: Coincident(g2,g3)
    c: Coincident(g3,g0)
    c: Horizontal(g2)
    c: Vertical(g3)
    c: DistanceX(g0,g0) = 65
    c: DistanceY(g1,g1) = 30
    c: Symmetric(g0,g0,g-2)
    c: Symmetric(g0,g1,g-1)
    c: Coincident(g4,g5)
    c: Coincident(g5,g6)
    c: Coincident(g6,g7)
    c: Coincident(g7,g4)
    c: Horizontal(g4)
    c: Horizontal(g6)
    c: Vertical(g5)
    c: Vertical(g7)
    c: DistanceX(g4,g4) = 58
    c: DistanceY(g5,g5) = 23
    c: Symmetric(g4,g5,g-1)
    c: Symmetric(g4,g4,g-2)
    c: Coincident(g8,g4)
    c: Coincident(g9,g4)
    c: Coincident(g10,g5)
    c: Coincident(g11,g6)
    c: Radius(g11) = 1.375
    c: Radius(g8) = 1.375
    c: Radius(g9) = 1.375
    c: Radius(g10) = 1.375
    c: Coincident(g12,g13)
    c: Coincident(g13,g14)
    c: Coincident(g14,g15)
    c: Coincident(g15,g12)
    c: Horizontal(g12)
    c: Horizontal(g14)
    c: Vertical(g13)
    c: Vertical(g15)
    c: DistanceX(g4,g12) = 0.5
    c: DistanceY(g4,g12) = 0.5
    c: DistanceY(g13,g5) = 0.5
    c: DistanceX(g14,g6) = 0.5
    c: Coincident(g16,g12)
    c: Radius(g16) = 3
    c: Coincident(g17,g12)
    c: Radius(g17) = 3
    c: Coincident(g18,g13)
    c: Radius(g18) = 3
    c: Coincident(g19,g14)
    c: Radius(g19) = 3
    c: PointOnObject(g16,g0)
    c: PointOnObject(g17,g1)
    c: PointOnObject(g18,g2)
    c: PointOnObject(g19,g3)
    c: Coincident(g20,g16)
    c: Horizontal(g20)
    c: Coincident(g20,g17)
    c: Coincident(g21,g17)
    c: Vertical(g21)
    c: Coincident(g18,g21)
    c: Coincident(g22,g18)
    c: Horizontal(g22)
    c: Coincident(g19,g22)
    c: Coincident(g23,g19)
    c: Vertical(g23)
    c: Coincident(g23,g16)
    c: Vertical(g24)
    c: DistanceX(g24,g4) = 2.6
    c: Tangent(g25,g28) = 1.5708
    c: Tangent(g25,g27) = -1.5708
    c: Tangent(g27,g26) = -1.5708
    c: Tangent(g28,g26) = 1.5708
    c: Vertical(g27)
    c: Equal(g25,g26)
    c: PointOnObject(g25,g24)
    c: DistanceX(g26,g26) = 1.5
    c: Horizontal(g29)
    c: DistanceY(g29,g4) = 8.16
    c: Coincident(g30,g31)
    c: Coincident(g31,g32)
    c: Coincident(g32,g33)
    c: Coincident(g33,g30)
    c: Horizontal(g30)
    c: Horizontal(g32)
    c: Vertical(g31)
    c: Vertical(g33)
    c: DistanceY(g33,g33) = 11
    c: DistanceY(g29,g30) = 5.5
    c: DistanceX(g30,g30) = 2
    c: DistanceY(g26,g25) = 9.5
    c: Symmetric(g25,g26,g29)
FEATURE [Part::Feature] path76
  shape: bbox 67.53 x 33.36 x 2e-07 mm, 1 faces, 0 solids (baked)
FEATURE [Part::Feature] path76001
  shape: bbox 56.51 x 33.36 x 2e-07 mm, 1 faces, 0 solids (baked)
FEATURE [Part::Feature] path76002
  shape: bbox 67.23 x 33.39 x 2e-07 mm, 1 faces, 0 solids (baked)
FEATURE [Part::Feature] path76003
  shape: bbox 86.8 x 33.05 x 2e-07 mm, 1 faces, 0 solids (baked)
FEATURE [Part::Feature] path76004
  shape: bbox 24.36 x 17.06 x 2e-07 mm, 1 faces, 0 solids (baked)
FEATURE [Part::Cut] Cut
  Base = -> path76003
  Tool = -> path76004
FEATURE [Part::MultiFuse] Fusion
  Shapes = -> [path76,path76001,path76002,Cut]
FEATURE [Part::FeaturePython] Scale001  # Draft clone (typed FeaturePython)
  Fuse = false
  Objects = -> [Fusion]
  Placement = pos=(-20,0,14.85) rot=(0,0,1;0rad)
  Scale = (0.18,0.18,0.18)
FEATURE [Part::Extrusion] Extrude
  Base = -> Scale001
  Dir = (0,0,1)
  DirMode = 0
  FaceMakerClass = Part::FaceMakerBullseye
  LengthFwd = 5
  LengthRev = 0
  Solid = false
  Symmetric = false
FEATURE [Mesh::Feature] Mesh  label="Cut001 (Meshed)"
FEATURE [PartDesign::Body] Body
  Group = -> [Sketch,Sketch001,Pad,Sketch002,Pocket,Sketch003,Pocket001,Sketch004,Sketch005,Pocket002,Sketch006,Pocket003,Fillet,Chamfer,Sketch007,Hole,Sketch008,Pocket004,Fillet002,Pocket006,Sketch009,Fillet003,Sketch010,Fillet004]
  Origin = -> Origin
  Tip = -> Fillet004
FEATURE [PartDesign::Fillet] Fillet003
  Base = -> Pocket006 [Edge38,Edge33,Edge34,Edge20,Edge21,Edge24,Edge23,Edge96,Edge90,Edge94,Edge116,Edge88,Edge114,Edge124]
  BaseFeature = -> Pocket006
  Radius = 0.15
FEATURE [Sketcher::SketchObject] Sketch010
  MapMode = 5
  Placement = pos=(0,0,15.5) rot=(0,0,1;0rad)
  Support = -> [Fillet003]
  expr: Constraints[7] = Sketch.Constraints[9]
  expr: Constraints[40] = Sketch.Constraints[42]
  expr: Constraints[18] = Sketch.Constraints[20]
  expr: Constraints[19] = Sketch.Constraints[21]
  expr: Constraints[29] = Sketch.Constraints[31]
  expr: Constraints[27] = Sketch.Constraints[29]
  expr: Constraints[28] = Sketch.Constraints[30]
  expr: Constraints[26] = Sketch.Constraints[28]
  expr: Constraints[6] = Sketch.Constraints[8]
  expr: Constraints[38] = Sketch.Constraints[40]
  expr: Constraints[47] = Sketch.Constraints[49]
  expr: Constraints[39] = Sketch.Constraints[41]
  expr: Constraints[49] = Sketch.Constraints[51]
  expr: Constraints[45] = Sketch.Constraints[47]
  expr: Constraints[43] = Sketch.Constraints[45]
  expr: Constraints[41] = Sketch.Constraints[43]
  sketch-geometry (62):
    g0: LineSegment [constr] StartX=-32.5 StartY=15 StartZ=0 EndX=32.5 EndY=15 EndZ=0
    g1: LineSegment [constr] StartX=32.5 StartY=15 StartZ=0 EndX=32.5 EndY=-15 EndZ=0
    g2: LineSegment [constr] StartX=32.5 StartY=-15 StartZ=0 EndX=-32.5 EndY=-15 EndZ=0
    g3: LineSegment [constr] StartX=-32.5 StartY=-15 StartZ=0 EndX=-32.5 EndY=15 EndZ=0
    g4: LineSegment [constr] StartX=-29 StartY=11.5 StartZ=0 EndX=29 EndY=11.5 EndZ=0
    g5: LineSegment [constr] StartX=29 StartY=11.5 StartZ=0 EndX=29 EndY=-11.5 EndZ=0
    g6: LineSegment [constr] StartX=29 StartY=-11.5 StartZ=0 EndX=-29 EndY=-11.5 EndZ=0
    g7: LineSegment [constr] StartX=-29 StartY=-11.5 StartZ=0 EndX=-29 EndY=11.5 EndZ=0
    g8: Circle [constr] CenterX=-29 CenterY=11.5 CenterZ=0 NormalX=0 NormalY=0 NormalZ=1 AngleXU=0 Radius=1.375
    g9: Circle [constr] CenterX=29 CenterY=11.5 CenterZ=0 NormalX=0 NormalY=0 NormalZ=1 AngleXU=0 Radius=1.375
    g10: Circle [constr] CenterX=29 CenterY=-11.5 CenterZ=0 NormalX=0 NormalY=0 NormalZ=1 AngleXU=0 Radius=1.375
    g11: Circle [constr] CenterX=-29 CenterY=-11.5 CenterZ=0 NormalX=0 NormalY=0 NormalZ=1 AngleXU=0 Radius=1.375
    g12: LineSegment [constr] StartX=-29.5 StartY=12 StartZ=0 EndX=29.5 EndY=12 EndZ=0
    g13: LineSegment [constr] StartX=29.5 StartY=12 StartZ=0 EndX=29.5 EndY=-12 EndZ=0
    g14: LineSegment [constr] StartX=29.5 StartY=-12 StartZ=0 EndX=-29.5 EndY=-12 EndZ=0
    g15: LineSegment [constr] StartX=-29.5 StartY=-12 StartZ=0 EndX=-29.5 EndY=12 EndZ=0
    g16: ArcOfCircle [constr] CenterX=-29.5 CenterY=12 CenterZ=0 NormalX=0 NormalY=0 NormalZ=1 AngleXU=0 Radius=3 StartAngle=1.5708 EndAngle=3.14159
    g17: ArcOfCircle [constr] CenterX=29.5 CenterY=12 CenterZ=0 NormalX=0 NormalY=0 NormalZ=1 AngleXU=0 Radius=3 StartAngle=5.0002e-08 EndAngle=1.5708
    g18: ArcOfCircle [constr] CenterX=29.5 CenterY=-12 CenterZ=0 NormalX=0 NormalY=0 NormalZ=1 AngleXU=0 Radius=3 StartAngle=4.71239 EndAngle=6.28319
    g19: ArcOfCircle [constr] CenterX=-29.5 CenterY=-12 CenterZ=0 NormalX=0 NormalY=0 NormalZ=1 AngleXU=0 Radius=3 StartAngle=3.14159 EndAngle=4.71239
    g20: LineSegment [constr] StartX=-29.5 StartY=15 StartZ=0 EndX=29.5 EndY=15 EndZ=0
    g21: LineSegment [constr] StartX=32.5 StartY=12 StartZ=0 EndX=32.5 EndY=-12 EndZ=0
    g22: LineSegment [constr] StartX=29.5 StartY=-15 StartZ=0 EndX=-29.5 EndY=-15 EndZ=0
    g23: LineSegment [constr] StartX=-32.5 StartY=-12 StartZ=0 EndX=-32.5 EndY=12 EndZ=0
    g24: LineSegment [constr] StartX=25.3417 StartY=8.13712 StartZ=0 EndX=27.8417 EndY=8.13712 EndZ=0
    g25: LineSegment [constr] StartX=27.8417 StartY=8.13712 StartZ=0 EndX=27.8417 EndY=-1.46288 EndZ=0
    g26: LineSegment [constr] StartX=27.8417 StartY=-1.46288 StartZ=0 EndX=25.3417 EndY=-1.46288 EndZ=0
    g27: LineSegment [constr] StartX=25.3417 StartY=-1.46288 StartZ=0 EndX=25.3417 EndY=8.13712 EndZ=0
    g28: LineSegment [constr] StartX=25.3417 StartY=6.93712 StartZ=0 EndX=27.8417 EndY=6.93712 EndZ=0
    g29: LineSegment [constr] StartX=25.3417 StartY=5.73712 StartZ=0 EndX=27.8417 EndY=5.73712 EndZ=0
    g30: LineSegment [constr] StartX=25.3417 StartY=4.53712 StartZ=0 EndX=27.8417 EndY=4.53712 EndZ=0
    g31: LineSegment [constr] StartX=25.3417 StartY=3.33712 StartZ=0 EndX=27.8417 EndY=3.33712 EndZ=0
    g32: LineSegment [constr] StartX=25.3417 StartY=2.13712 StartZ=0 EndX=27.8417 EndY=2.13712 EndZ=0
    g33: LineSegment [constr] StartX=25.3417 StartY=0.937121 StartZ=0 EndX=27.8417 EndY=0.937121 EndZ=0
    g34: LineSegment [constr] StartX=25.3417 StartY=-0.262879 StartZ=0 EndX=27.8417 EndY=-0.262879 EndZ=0
    g35: ArcOfCircle CenterX=25.3417 CenterY=8.13712 CenterZ=0 NormalX=0 NormalY=0 NormalZ=1 AngleXU=0 Radius=0.75 StartAngle=1.12328 EndAngle=4.26487
    g36: ArcOfCircle CenterX=27.8417 CenterY=6.93712 CenterZ=0 NormalX=0 NormalY=0 NormalZ=1 AngleXU=0 Radius=0.75 StartAngle=4.26487 EndAngle=7.40646
    g37: Circle [constr] CenterX=27.8417 CenterY=6.93712 CenterZ=0 NormalX=0 NormalY=0 NormalZ=1 AngleXU=0 Radius=0.75
    g38: Circle [constr] CenterX=25.3417 CenterY=8.13712 CenterZ=0 NormalX=0 NormalY=0 NormalZ=1 AngleXU=0 Radius=0.75
    g39: LineSegment [constr] StartX=25.4338 StartY=8.92483 StartZ=0 EndX=28.7439 EndY=7.33601 EndZ=0
    g40: LineSegment [constr] StartX=24.2457 StartY=7.83129 StartZ=0 EndX=27.5618 EndY=6.23954 EndZ=0
    g41: LineSegment StartX=25.6663 StartY=8.81326 StartZ=0 EndX=28.1663 EndY=7.61326 EndZ=0
    g42: LineSegment StartX=25.0172 StartY=7.46098 StartZ=0 EndX=27.5172 EndY=6.26098 EndZ=0
    g43: ArcOfCircle CenterX=25.3417 CenterY=5.73712 CenterZ=0 NormalX=0 NormalY=0 NormalZ=1 AngleXU=0 Radius=0.75 StartAngle=1.12852 EndAngle=4.25962
    g44: LineSegment StartX=25.6627 StartY=6.41496 StartZ=0 EndX=28.149 EndY=5.22128 EndZ=0
    g45: ArcOfCircle CenterX=27.8417 CenterY=4.53712 CenterZ=0 NormalX=0 NormalY=0 NormalZ=1 AngleXU=0 Radius=0.75 StartAngle=4.23957 EndAngle=7.43184
    g46: LineSegment StartX=25.0136 StartY=5.06269 StartZ=0 EndX=27.5002 EndY=3.86941 EndZ=0
    g47: Circle CenterX=25.3417 CenterY=-1.46288 CenterZ=0 NormalX=0 NormalY=0 NormalZ=1 AngleXU=0 Radius=0.75
    g48: Circle CenterX=27.8417 CenterY=-0.262879 CenterZ=0 NormalX=0 NormalY=0 NormalZ=1 AngleXU=0 Radius=0.75
    g49: Circle CenterX=25.3417 CenterY=0.937121 CenterZ=0 NormalX=0 NormalY=0 NormalZ=1 AngleXU=0 Radius=0.75
    g50: Circle CenterX=27.8417 CenterY=2.13712 CenterZ=0 NormalX=0 NormalY=0 NormalZ=1 AngleXU=0 Radius=0.75
    g51: Circle CenterX=25.3417 CenterY=3.33712 CenterZ=0 NormalX=0 NormalY=0 NormalZ=1 AngleXU=0 Radius=0.75
    g52: LineSegment [constr] StartX=25.8911 StartY=-2.0311 StartZ=0 EndX=28.1814 EndY=-0.931754 EndZ=0
    g53: LineSegment [constr] StartX=24.1632 StartY=-1.19664 StartZ=0 EndX=27.4908 EndY=0.400624 EndZ=0
    g54: LineSegment [constr] StartX=24.363 StartY=0.574977 StartZ=0 EndX=28.2413 EndY=-1.28662 EndZ=0
    g55: LineSegment [constr] StartX=25.6678 StartY=1.61253 StartZ=0 EndX=28.5751 EndY=0.217016 EndZ=0
    g56: LineSegment [constr] StartX=24.9997 StartY=-0.0589725 StartZ=0 EndX=28.6995 EndY=1.71693 EndZ=0
    g57: LineSegment [constr] StartX=24.1511 StartY=1.19754 StartZ=0 EndX=27.2971 EndY=2.70762 EndZ=0
    g58: LineSegment [constr] StartX=24.3738 StartY=2.96979 StartZ=0 EndX=27.5399 EndY=1.45005 EndZ=0
    g59: Circle [constr] CenterX=25.3417 CenterY=2.13712 CenterZ=0 NormalX=0 NormalY=0 NormalZ=1 AngleXU=0 Radius=0.331828
    g60: Circle [constr] CenterX=27.8417 CenterY=0.937121 CenterZ=0 NormalX=0 NormalY=0 NormalZ=1 AngleXU=0 Radius=0.331828
    g61: Circle [constr] CenterX=25.3417 CenterY=-0.262879 CenterZ=0 NormalX=0 NormalY=0 NormalZ=1 AngleXU=0 Radius=0.331828
  constraints (163):
    c: Coincident(g0,g1)
    c: Coincident(g1,g2)
    c: Coincident(g2,g3)
    c: Coincident(g3,g0)
    c: Horizontal(g2)
    c: Vertical(g3)
    c: DistanceX(g0,g0) = 65
    c: DistanceY(g1,g1) = 30
    c: Symmetric(g0,g0,g-2)
    c: Symmetric(g0,g1,g-1)
    c: Coincident(g4,g5)
    c: Coincident(g5,g6)
    c: Coincident(g6,g7)
    c: Coincident(g7,g4)
    c: Horizontal(g4)
    c: Horizontal(g6)
    c: Vertical(g5)
    c: Vertical(g7)
    c: DistanceX(g4,g4) = 58
    c: DistanceY(g5,g5) = 23
    c: Symmetric(g4,g5,g-1)
    c: Symmetric(g4,g4,g-2)
    c: Coincident(g8,g4)
    c: Coincident(g9,g4)
    c: Coincident(g10,g5)
    c: Coincident(g11,g6)
    c: Radius(g11) = 1.375
    c: Radius(g8) = 1.375
    c: Radius(g9) = 1.375
    c: Radius(g10) = 1.375
    c: Coincident(g12,g13)
    c: Coincident(g13,g14)
    c: Coincident(g14,g15)
    c: Coincident(g15,g12)
    c: Horizontal(g12)
    c: Horizontal(g14)
    c: Vertical(g13)
    c: Vertical(g15)
    c: DistanceX(g4,g12) = 0.5
    c: DistanceY(g4,g12) = 0.5
    c: DistanceY(g13,g5) = 0.5
    c: DistanceX(g14,g6) = 0.5
    c: Coincident(g16,g12)
    c: Radius(g16) = 3
    c: Coincident(g17,g12)
    c: Radius(g17) = 3
    c: Coincident(g18,g13)
    c: Radius(g18) = 3
    c: Coincident(g19,g14)
    c: Radius(g19) = 3
    c: PointOnObject(g16,g0)
    c: PointOnObject(g17,g1)
    c: PointOnObject(g18,g2)
    c: PointOnObject(g19,g3)
    c: Coincident(g20,g16)
    c: Horizontal(g20)
    c: Coincident(g20,g17)
    c: Coincident(g21,g17)
    c: Vertical(g21)
    c: Coincident(g18,g21)
    c: Coincident(g22,g18)
    c: Horizontal(g22)
    c: Coincident(g19,g22)
    c: Coincident(g23,g19)
    c: Vertical(g23)
    c: Coincident(g23,g16)
    c: Coincident(g24,g25)
    c: Coincident(g25,g26)
    c: Coincident(g26,g27)
    c: Coincident(g27,g24)
    c: Horizontal(g24)
    c: Horizontal(g26)
    c: Vertical(g25)
    c: Vertical(g27)
    c: DistanceX(g4,g24) = 54.3417  '3,362879'
    c: DistanceX(g24,g24) = 2.5
    c: DistanceY(g27,g27) = 9.6
    c: DistanceY(g24,g4) = 3.36288
    c: Horizontal(g28)
    c: Horizontal(g29)
    c: Horizontal(g30)
    c: Horizontal(g32)
    c: Horizontal(g33)
    c: DistanceY(g28,g24) = 1.2
    c: DistanceY(g29,g28) = 1.2
    c: DistanceY(g30,g29) = 1.2
    c: DistanceY(g31,g30) = 1.2
    c: DistanceY(g32,g31) = 1.2
    c: DistanceY(g33,g32) = 1.2
    c: Horizontal(g34)
    c: DistanceY(g34,g33) = 1.2
    c: PointOnObject(g28,g27)
    c: PointOnObject(g29,g27)
    c: PointOnObject(g30,g27)
    c: PointOnObject(g31,g27)
    c: PointOnObject(g32,g27)
    c: PointOnObject(g33,g27)
    c: PointOnObject(g34,g27)
    c: PointOnObject(g34,g25)
    c: PointOnObject(g33,g25)
    c: PointOnObject(g32,g25)
    c: PointOnObject(g31,g25)
    c: PointOnObject(g30,g25)
    c: PointOnObject(g29,g25)
    c: PointOnObject(g28,g25)
    c: Coincident(g35,g24)
    c: Coincident(g36,g28)
    c: Radius(g35) = 0.75
    c: Radius(g36) = 0.75
    c: Coincident(g37,g28)
    c: Coincident(g38,g24)
    c: Radius(g38) = 0.75
    c: Radius(g37) = 0.75
    c: Tangent(g39,g37)
    c: Tangent(g39,g38)
    c: Tangent(g40,g38)
    c: Tangent(g40,g37)
    c: PointOnObject(g41,g39)
    c: PointOnObject(g41,g39)
    c: PointOnObject(g42,g40)
    c: PointOnObject(g42,g40)
    c: Coincident(g41,g35)
    c: Coincident(g35,g42)
    c: Coincident(g41,g36)
    c: Coincident(g36,g42)
    c: Equal(g35,g43) = 0.75
    c: Equal(g36,g45) = 0.75
    c: Coincident(g44,g43)
    c: Coincident(g43,g46)
    c: Coincident(g44,g45)
    c: Coincident(g45,g46)
    c: Coincident(g43,g29)
    c: Coincident(g45,g30)
    c: Coincident(g48,g34)
    c: Coincident(g49,g33)
    c: Coincident(g50,g32)
    c: Coincident(g51,g31)
    c: Radius(g51) = 0.75
    c: Radius(g50) = 0.75
    c: Radius(g49) = 0.75
    c: Radius(g48) = 0.75
    c: Radius(g47) = 0.75
    c: Tangent(g55,g48)
    c: Tangent(g55,g49)
    c: Tangent(g54,g49)
    c: Tangent(g54,g48)
    c: Tangent(g53,g47)
    c: Tangent(g53,g48)
    c: Coincident(g47,g26)
    c: Tangent(g47,g52)
    c: Tangent(g52,g48)
    c: Tangent(g56,g49)
    c: Tangent(g56,g50)
    c: Tangent(g57,g50)
    c: Tangent(g57,g49)
    c: Tangent(g58,g51)
    c: Tangent(g58,g50)
    c: Coincident(g59,g32)
    c: Tangent(g59,g58)
    c: Coincident(g60,g33)
    c: Tangent(g60,g56)
    c: Coincident(g61,g34)
    c: Tangent(g61,g54)
FEATURE [PartDesign::Pocket] Pocket006
  BaseFeature = -> Fillet002
  Length = 5
  Length2 = 100
  Profile = -> Sketch010
  Type = 2
FEATURE [PartDesign::Fillet] Fillet004
  Base = -> Fillet003 [Edge248,Edge241,Edge247,Edge249,Edge236]
  BaseFeature = -> Fillet003
  Radius = 0.1
FEATURE [Part::Cut] Cut001
  Base = -> Fillet004
  Tool = -> Extrude
